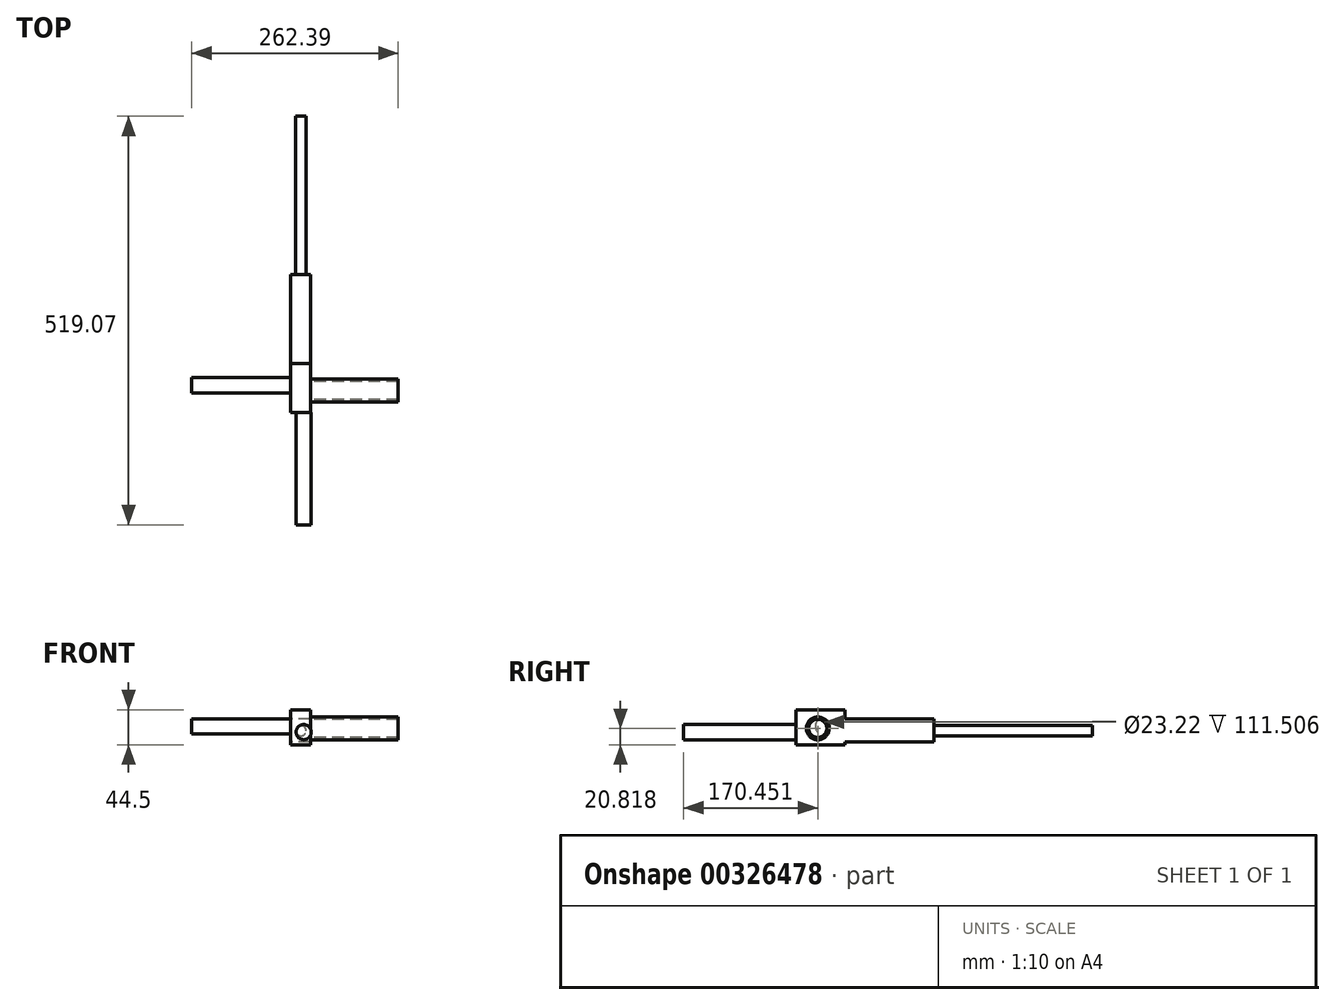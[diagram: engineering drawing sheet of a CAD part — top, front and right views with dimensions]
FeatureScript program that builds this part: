
annotation { "Feature Type Name" : "Feature", "Feature Type Description" : "" }
export const myFeature = defineFeature(function(context is Context, id is Id, definition is map)
    precondition{}
    {
        {
            var Q0;
            Q0=qCreatedBy(makeId("Right.planeOp"),FACE);
            var sketch = newSketch(context, id + "F0", { "sketchPlane" : qUnion([Q0])});
            skLineSegment(sketch, "E0.bottom", {"start": v(0, 0) * mm, "end": v(62.63, 0) * mm});
            skLineSegment(sketch, "E0.top", {"start": v(0, -44.5) * mm, "end": v(62.63, -44.5) * mm});
            skLineSegment(sketch, "E0.left", {"start": v(0, 0) * mm, "end": v(0, -44.5) * mm});
            skLineSegment(sketch, "E0.right", {"start": v(62.63, 0) * mm, "end": v(62.63, -44.5) * mm});
            skSolve(sketch);
        }
        {
            var Q0;
            Q0 = qSketchRegion(id + "F0", true);
            extrude(context, id + "F1", {"entities" : qUnion([Q0]), "depth" : 25.4 * mm});
        }
        {
            var Q0;
            Q0=makeQuery(id+"F1.opExtrude","SWEPT_FACE",FACE,{"disambiguationData":[OSD([sQuery(id+"F0.wireOp",EDGE,"E0.left")])]});
            var sketch = newSketch(context, id + "F2", { "sketchPlane" : qUnion([Q0])});
            skCircle(sketch, "E1", {"center": v(16.75, -28.45) * mm, "radius": 9.6 * mm});
            skPoint(sketch, "E1.first.point", {"position": v(11.98, -20.1) * mm});
            skPoint(sketch, "E1.second.point", {"position": v(12.7, -37.16) * mm});
            skPoint(sketch, "E1.second.point.positionSnap0", {"position": v(12.7, -44.5) * mm});
            skPoint(sketch, "E1.third.point", {"position": v(18.91, -19.08) * mm});
            skSolve(sketch);
        }
        {
            var Q0;
            Q0 = qSketchRegion(id + "F2", true);
            extrude(context, id + "F3", {"entities" : qUnion([Q0]), "operationType" : NewBodyOperationType.ADD, "depth" : 142.5 * mm});
        }
        {
            var Q0;
            Q0=makeQuery(id+"F1.opExtrude","CAP_FACE",FACE,{"disambiguationData":[OSD([sQuery(id+"F0.wireOp",EDGE,"E0.bottom"),sQuery(id+"F0.wireOp",EDGE,"E0.top"),sQuery(id+"F0.wireOp",EDGE,"E0.left"),sQuery(id+"F0.wireOp",EDGE,"E0.right")])],"isStart":false});
            var sketch = newSketch(context, id + "F4", { "sketchPlane" : qUnion([Q0])});
            skCircle(sketch, "E2", {"center": v(27.96, -23.68) * mm, "radius": 11.6 * mm});
            skCircle(sketch, "E3", {"center": v(27.96, -23.68) * mm, "radius": 14.48 * mm});
            skSolve(sketch);
        }
        {
            var Q0;
            Q0 = qSketchRegion(id + "F4", true);
            extrude(context, id + "F5", {"entities" : qUnion([Q0]), "operationType" : NewBodyOperationType.ADD, "depth" : 111.5 * mm});
        }
        {
            var Q0;
            Q0=makeQuery(id+"F1.opExtrude","CAP_FACE",FACE,{"disambiguationData":[OSD([sQuery(id+"F0.wireOp",EDGE,"E0.bottom"),sQuery(id+"F0.wireOp",EDGE,"E0.top"),sQuery(id+"F0.wireOp",EDGE,"E0.left"),sQuery(id+"F0.wireOp",EDGE,"E0.right")])],"isStart":true});
            var sketch = newSketch(context, id + "F6", { "sketchPlane" : qUnion([Q0])});
            skCircle(sketch, "E4", {"center": v(-34.52, -21.09) * mm, "radius": 9.73 * mm});
            skSolve(sketch);
        }
        {
            var Q0;
            Q0 = qSketchRegion(id + "F6", true);
            extrude(context, id + "F7", {"entities" : qUnion([Q0]), "operationType" : NewBodyOperationType.ADD, "depth" : 125.48 * mm});
        }
        {
            var Q0;
            Q0=makeQuery(id+"F1.opExtrude","SWEPT_FACE",FACE,{"disambiguationData":[OSD([sQuery(id+"F0.wireOp",EDGE,"E0.right")])]});
            var sketch = newSketch(context, id + "F8", { "sketchPlane" : qUnion([Q0])});
            skLineSegment(sketch, "E5.bottom", {"start": v(-25.4, -11.58) * mm, "end": v(0, -11.58) * mm});
            skLineSegment(sketch, "E5.top", {"start": v(-25.4, -41.14) * mm, "end": v(0, -41.14) * mm});
            skLineSegment(sketch, "E5.left", {"start": v(-25.4, -11.58) * mm, "end": v(-25.4, -41.14) * mm});
            skLineSegment(sketch, "E5.right", {"start": v(0, -11.58) * mm, "end": v(0, -41.14) * mm});
            skSolve(sketch);
        }
        {
            var Q0;
            Q0 = qSketchRegion(id + "F8", true);
            extrude(context, id + "F9", {"entities" : qUnion([Q0]), "operationType" : NewBodyOperationType.ADD, "depth" : 112.78 * mm});
        }
        {
            var Q0;
            Q0=makeQuery(id+"F9.opExtrude","CAP_FACE",FACE,{"disambiguationData":[OSD([sQuery(id+"F8.wireOp",EDGE,"E5.bottom"),sQuery(id+"F8.wireOp",EDGE,"E5.top"),sQuery(id+"F8.wireOp",EDGE,"E5.left"),sQuery(id+"F8.wireOp",EDGE,"E5.right")])],"isStart":false});
            var sketch = newSketch(context, id + "F10", { "sketchPlane" : qUnion([Q0])});
            skCircle(sketch, "E6", {"center": v(-13.26, -26.68) * mm, "radius": 6.58 * mm});
            skSolve(sketch);
        }
        {
            var Q0;
            Q0 = qSketchRegion(id + "F10", true);
            extrude(context, id + "F11", {"entities" : qUnion([Q0]), "operationType" : NewBodyOperationType.ADD, "depth" : 201.17 * mm});
        }
    });
